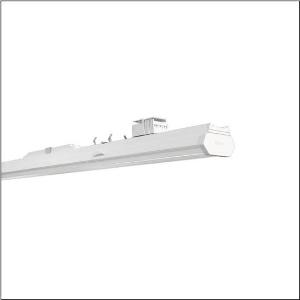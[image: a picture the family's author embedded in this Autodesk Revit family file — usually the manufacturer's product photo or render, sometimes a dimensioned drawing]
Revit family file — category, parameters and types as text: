
# Revit family: licross_r__11_protected_ho_51tp11dn4f5s_1ce9
name_source: partatom
category: Lighting Fixtures
units: mm (PartAtom-declared; Revit-internal decimal feet)

## family parameters
Cut with Voids When Loaded = No
Host = Face
Light Source = No
Part Type = Normal
Room Calculation Point = No
Round Connector Dimension = Use Diameter
Shared = No

## types (1)
- --- (1 x LED, 15510 lm, 87.3 W, 4000K)
    Apparent Load = 87 VA
    CIE Flux Codes = 84 94 98 99 100
    Color Rendering = 80
    Color Temperature = 4000K
    Default Elevation = 1800 mm
    Description = Licross® 11 Protected HO, luminaire insert, of sheet steel, galvanised, coil coated, white, length: 1.500mm, width: 90mm, height: 101mm, LED rated luminous flux: 15.510lm, light colour: 840, control gear: DALI 2, with plug, 5-pole, with phase selection, mains connection: 220..240V, AC, 50/60Hz, rated input power: 87W, halogen-free wiring, primary light control with lens, of plastic, primary optical cover: cover, of PMMA, light emission: direct distribution, primary light characteristic: symmetric, protection rating (complete): IP64, insulation class (complete): insulation class I (protective earthing), certification: CE, ENEC, VDE, UKCA, protection symbol: D if used in an environment with conductive dust loads with corresponding accessories, impact resistance: IK06, permissible ambient temperature for indoor applications: -25..+30°C, corresponds to IFS (International Featured Standards) requirements for safety and quality in the food industry, reducing of maximum allowable ambient temperature of 5°C with ceiling mounting, LABS conformity tested according to VDMA 24364:2018-05, packaging unit: 1 piece
    Height = 92 mm
    Lamp = 1 x LED
    Lamp Light Flux = 15510 lm
    Lamp Power = 87.3 W
    Lamp count = 1
    Length = 1500 mm
    Luminous efficacy = 178 lm/W
    Manufacturer = Siteco
    ModVariant = No
    Model = 51TP11DN4F5S
    Mounting Place = Ceiling
    Mounting Type = Pendant
    Number of Poles = 1
    OnlyDefault = Yes
    Power Factor = 1
    Product Name = Licross® 11 Protected HO
    Product group = luminaire insert
    ProductGroupID = 901
    Protection Class = Protection class I
    Protection Degree = IP 64
    RLX_Detail_Level = 1
    RLX_Emergency_Light_Flux = 0 lm
    RLX_Emergency_Type = 0
    RLX_Emergency_Type_DB = No
    RlxData = <blob elided: 24441 chars, md5=19f25977>
    Socket = socket
    Standby Power = 0 W
    System Light Flux = 15510 lm
    System Power = 87 W
    Type Comments = factory setting: luminous flux: 100 % | dim-lin: 254 | 589 mA
    Type Image = l_1256148.jpg
    URL = http://relux.com
    VarID = @adj_049299
    Voltage = 0 V
    Weight = 0.00 kg
    Width = 88 mm

## geometry (parser evidence)
native form markers: Blend x4, Sweep x11
no freeform markers — native parametric forms only
